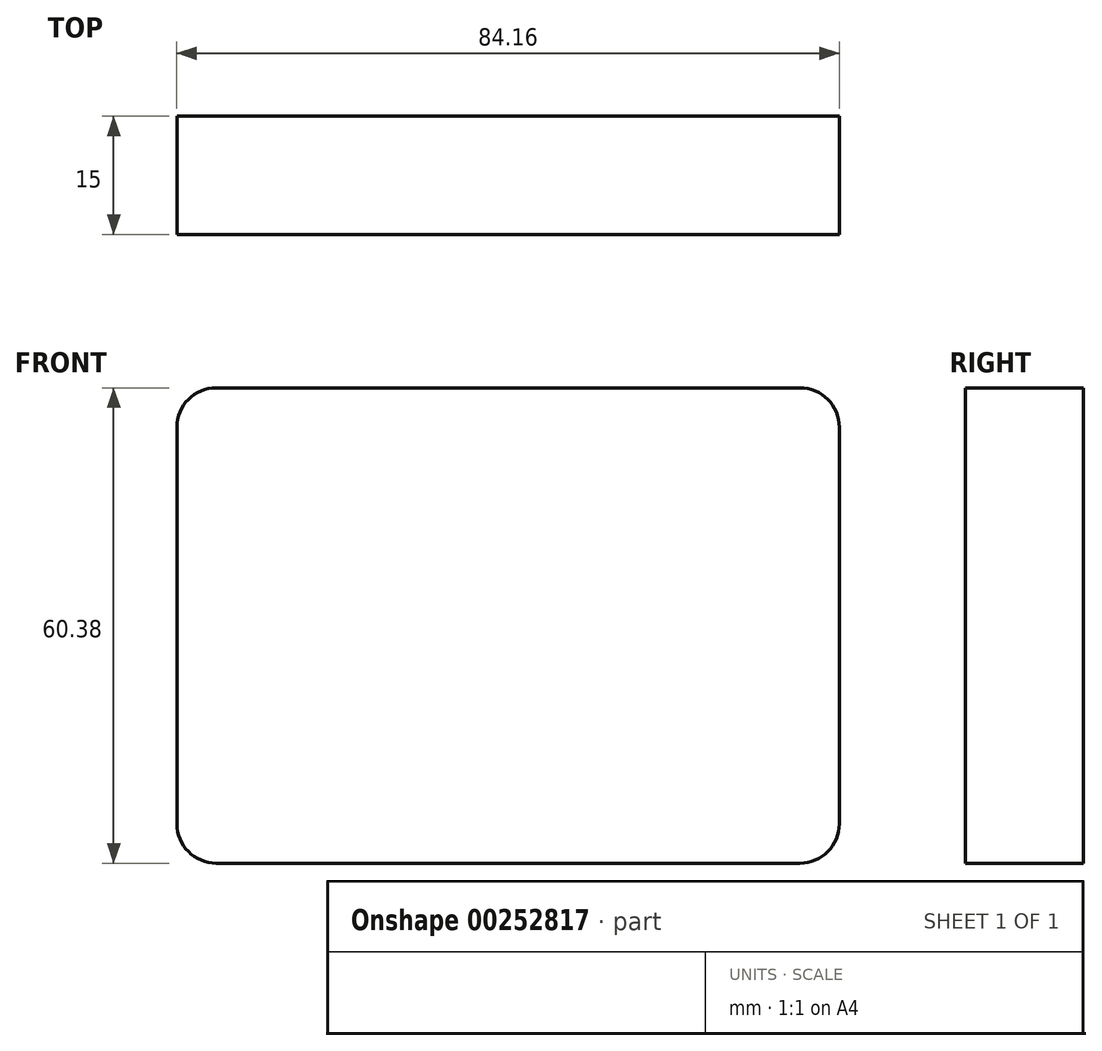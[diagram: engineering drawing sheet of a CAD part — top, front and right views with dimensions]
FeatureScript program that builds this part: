
annotation { "Feature Type Name" : "Feature", "Feature Type Description" : "" }
export const myFeature = defineFeature(function(context is Context, id is Id, definition is map)
    precondition{}
    {
        {
            var Q0;
            Q0=qCreatedBy(makeId("Front.planeOp"),FACE);
            var sketch = newSketch(context, id + "F0", { "sketchPlane" : qUnion([Q0])});
            skLineSegment(sketch, "E0.bottom", {"start": v(-42.08, 30.19) * mm, "end": v(42.08, 30.19) * mm});
            skLineSegment(sketch, "E0.top", {"start": v(-42.08, -30.19) * mm, "end": v(42.08, -30.19) * mm});
            skLineSegment(sketch, "E0.left", {"start": v(-42.08, 30.19) * mm, "end": v(-42.08, -30.19) * mm});
            skLineSegment(sketch, "E0.right", {"start": v(42.08, 30.19) * mm, "end": v(42.08, -30.19) * mm});
            skPoint(sketch, "E0.middle", {"position": v(0, 0) * mm});
            skSolve(sketch);
        }
        {
            var Q0;
            Q0=makeQuery(id+"F0.imprint","IMPRINT",FACE,{"disambiguationData":[TD([[makeQuery(id+"F0.imprint","IMPRINT",EDGE,{"derivedFrom":sQuery(id+"F0.wireOp",EDGE,"E0.bottom")}),-1.0]])]});
            extrude(context, id + "F1", {"entities" : qUnion([Q0]), "endBound" : BoundingType.SYMMETRIC, "depth" : 15 * mm});
        }
        {
            var Q0;
            Q0=makeQuery(id+"F1.opExtrude","SWEPT_EDGE",EDGE,{"disambiguationData":[OSD([sQuery(id+"F0.wireOp",EDGE,"E0.bottom"),sQuery(id+"F0.wireOp",EDGE,"E0.left")])]});
            var Q1;
            Q1=makeQuery(id+"F1.opExtrude","SWEPT_EDGE",EDGE,{"disambiguationData":[OSD([sQuery(id+"F0.wireOp",EDGE,"E0.bottom"),sQuery(id+"F0.wireOp",EDGE,"E0.right")])]});
            var Q2;
            Q2=makeQuery(id+"F1.opExtrude","SWEPT_EDGE",EDGE,{"disambiguationData":[OSD([sQuery(id+"F0.wireOp",EDGE,"E0.top"),sQuery(id+"F0.wireOp",EDGE,"E0.right")])]});
            var Q3;
            Q3=makeQuery(id+"F1.opExtrude","SWEPT_EDGE",EDGE,{"disambiguationData":[OSD([sQuery(id+"F0.wireOp",EDGE,"E0.top"),sQuery(id+"F0.wireOp",EDGE,"E0.left")])]});
            fillet(context, id + "F2", {"entities" : qUnion([Q0, Q1, Q2, Q3]), "radius" : 5 * mm, "tangentPropagation" : true, "allowEdgeOverflow" : false});
        }
    });
